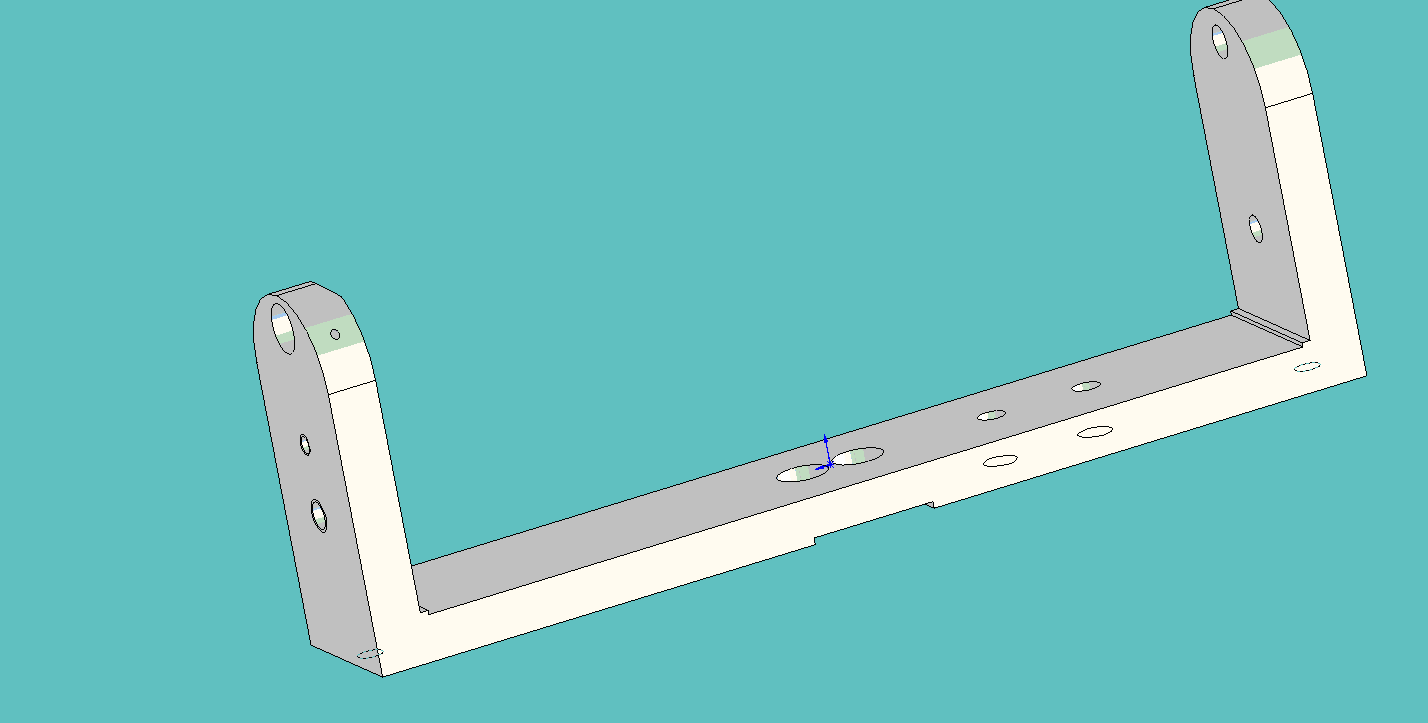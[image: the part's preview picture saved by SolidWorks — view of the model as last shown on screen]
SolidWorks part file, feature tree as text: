
SOLIDWORKS PART (.sldprt)
format: sldprt  version: not decoded by parser v0  size: 684,544 bytes
history: native  units: mm
features: sketch x22, hole x7, thread x6, plane x3, cut_extrude x2, material x1, extrude x1, chamfer x1, fillet x1 (+10 scaffold rows collapsed)
feature tree (54):
  scaffold x10  (default folders/planes/origin — collapsed)
  material  "Matériau <non spécifié>"
  plane  "Plan de face"
  plane  "Plan de dessus"
  plane  "Plan de droite"
  sketch  "Esquisse1"  dims[c1.D1=125.0mm c1.D2=113.0mm c1.D3=44.0mm c1.D4=5.5mm c1.D5=6.0mm c1.D6=1.0mm c1.D7=111.0mm c2.D7=4.7deg c3.D7=4.7mm c3.D8=15.1mm]
  extrude  "Extrusion1"  Depth=20mm
  chamfer  "Chanfrein2"  Distance=1mm Angle=45deg
  fillet  "Congé3"  Radius=10mm
  sketch  "Esquisse5"  dims[D1=20.5mm D2=12.0mm]
  hole  "Trou taraudé M4x0.73"  Diameter=3.3mm Depth=44mm
  sketch  "Esquisse3D4"
  sketch  "Esquisse6"  dims[hole-wizard template sketch: 59 standard entries collapsed; hole parameters kept: c18.Diamètre du trou pour taraudage jusqu'au prochain=3.3mm c18.Profondeur du trou pour taraudage jusqu'au prochain=44.0mm]
  thread  "Filetage de perçage7"  Diameter=4mm  [1 undecoded]
  thread  "Filetage de perçage8"  Diameter=4mm  [1 undecoded]
  sketch  "Esquisse7"  dims[D1=3.0mm]
  hole  "Trou taraudé M3x0.52"  Diameter=2.5mm Depth=7.5mm
  sketch  "Esquisse3D5"
  sketch  "Esquisse8"  dims[hole-wizard template sketch: 47 standard entries collapsed; hole parameters kept: c15.Profondeur du trou pour taraudage=7.5mm c15.D3=~14.816244mm c15.Angle de pointe=118.0deg]
  thread  "Filetage de perçage9"  Diameter=6mm  [1 undecoded]
  thread  "Filetage de perçage10"  Diameter=6mm  [1 undecoded]
  sketch  "Esquisse9"  dims[D1=17.5mm]
  hole  "Trou taraudé M4x0.74"  Diameter=3.3mm Depth=125mm
  sketch  "Esquisse3D6"
  sketch  "Esquisse10"  dims[hole-wizard template sketch: 59 standard entries collapsed; hole parameters kept: c18.Diamètre du trou pour taraudage jusqu'au prochain=3.3mm c18.Profondeur du trou pour taraudage jusqu'au prochain=125.0mm]
  thread  "Filetage de perçage11"  Diameter=4mm  [1 undecoded]
  sketch  "Esquisse11"  dims[D1=26.0mm]
  hole  "Trou taraudé M2.5x0.451"  Diameter=2.05mm Depth=21.35mm
  sketch  "Esquisse3D7"
  sketch  "Esquisse12"  dims[hole-wizard template sketch: 46 standard entries collapsed; hole parameters kept: c15.Diamètre du trou pour taraudage=2.05mm c15.Profondeur du trou pour taraudage=21.35mm c15.D3=~14.816244mm c15.Angle de pointe=118.0deg]
  thread  "Filetage de perçage12"  Diameter=6mm  [1 undecoded]
  sketch  "Esquisse13"  dims[D2=6.0mm D1=40.0mm]
  cut_extrude  "Enlèv. mat.-Extru.1"  Depth=20mm
  sketch  "Esquisse14"  dims[D1=4.0mm]
  cut_extrude  "Enlèv. mat.-Extru.2"  Depth=20mm
  sketch  "Esquisse15"  dims[D1=7.0mm]
  hole  "Chambrage pour vis à tête hexagonale M1.61"  Diameter=3.1mm Depth=5.5mm
  sketch  "Esquisse3D8"
  sketch  "Esquisse16"  dims[hole-wizard template sketch: 41 standard entries collapsed; hole parameters kept: c12.Diamètre du perçage jusqu'au prochain=3.1mm c12.Profondeur du perçage jusqu'au prochain=5.5mm c12.Diamètre du chambrage=6.0mm c12.Profondeur du chambrage=3.0mm]
  hole  "Dégagement M1.61"  Diameter=1mm Depth=5.5mm
  sketch  "Esquisse3D9"  dims[D1=40.0mm D2=3.0mm]
  sketch  "Esquisse19"  dims[hole-wizard template sketch: 46 standard entries collapsed; hole parameters kept: c15.Diamètre du perçage=1.0mm c15.Profondeur du perçage=5.5mm c15.D3=~14.816244mm c15.Angle de pointe=118.0deg]
  hole  "Dégagement M1.62"  Diameter=1mm Depth=5.5mm
  sketch  "Esquisse3D10"  dims[D1=3.0mm D2=40.0mm]
  sketch  "Esquisse20"  dims[hole-wizard template sketch: 46 standard entries collapsed; hole parameters kept: c15.Diamètre du perçage=1.0mm c15.Profondeur du perçage=5.5mm c15.D3=~14.816244mm c15.Angle de pointe=118.0deg]
decode coverage: 35 of 40 modeling features carry decoded parameters
note: ~ marks probable driven/reference dimensions
note: 6 parameter values undecoded
summary: Diameter pulled from absorbed wizard sketch
note: suppression state not decoded; provenance and decode notes live in map.json
